# Revit family: 08717100
name_source: partatom
category: Plumbing Fixtures
revit_build: Autodesk Revit 2018 (Build: 20170223_1515(x64)
units: mm (PartAtom-declared; Revit-internal decimal feet)

## family parameters
Always vertical = Yes
Cut with Voids When Loaded = No
OmniClass Number = 23.45.55.00
OmniClass Title = Sanitary Faucets, Wastes
Part Type = Normal
Room Calculation Point = No
Round Connector Dimension = Use Diameter
Shared = No
Work Plane-Based = No

## types (1)
- 08717100 Bath and shower faucet
    2D/3D/BIM Files URL = http://static.hansa.com
    3D View = https://static.hansa.com
    Additional Features = Retrofit safety lock 02000710 against scalding, can be ordered optionally. Limiter adjustable between 38°-42°C during mounting.
    Advanced Features = Inner body made of DZR brass
    Aerator = Standard aerator
    Approval DVGW = NW-6509CR0103
    AssetType = Fixed
    BIMObjectName = 08717100
    Backflow Prevention EN1717 = EB
    BodyMaterial = Brass
    Brand = HANSA
    Catalog Drawing URL = http://static.hansa.com
    Category = Health & Care
    CloseOffRating = 0
    Color = Chrome
    Connection = Eccentric coupling(s);Cover plate(s);Cover plate triple sealed
    Connection Size = G1/2
    Dimension Drawing URL = http://static.hansa.com
    Diverter = Turn operated diverter;Integrated into flow control handle
    DurationUnit = Year
    EAN Number = 4057304013454
    EN Standard = EN 1111
    ETIM Class Number = EC010862 Bath mixing tap
    FDV Document URL = http://www.hansa.com
    FaucetMainMaterial = Brass
    Features = Thermostatic
    Finish = Polished
    Flow Drawing URL = http://static.hansa.com
    Flow Rate At 300kPa = 4030.3 L/s
    FlowCoefficient = 0
    Group = Bath and shower faucet
    IfcExportAs = IfcValveType
    IfcExportType = FAUCET
    Installation Type = Wall mounted
    Installation Width = CC150± 15 mm
    Installation and Maintenance Guide URL = http://static.hansa.com
    Interactive AR View URL = https://static.hansa.com
    Lever Handle = Temperature control handle;Flow control handle;Eco feature for water flow
    Manufacturer = HANSA
    ManufacturerName = HANSA
    ManufacturerURL = http://www.hansa.com
    Market = International;Germany;Austria;Switzerland;Belgium;Netherlands;France;Czech Republic;Slovakia;Italy;Spain;Portugal;Australia
    Material = Brass
    Max. Hot Water Supply = 80 °C
    Mechanical Parts = Ceramic head part for flow control;Thermostatic cartridge for automatic temperature control;Non-return valve(s);Litter filter(s)
    Mobile Product Information URL = http://mpi.hansa.com
    Model = 08717100 Bath and shower faucet
    ModelReference = 08717100
    NBSDescription = Water supply fittings for baths
    NBSReference = 45-35-70/315
    Name = 08717100 Bath and shower faucet
    Name_en = 08717100 Bath and shower faucet
    Noise Class = II (ISO 3822)
    NominalDepth = 183 mm
    NominalHeight = 80 mm  [stored 0.262467 ft]
    NominalWidth = 290 mm
    Product Code = 08717100
    Product Family = HANSACARE Safety
    Product Image URL = http://static.hansa.com
    Product URL = http://static.hansa.com
    Revision = 3
    Sales Package dimensions (LxWxH) = 294 x 164 x 83
    Shape = Sculptured
    Size = 290x185x80 mm
    Spare-Part Information URL = http://static.hansa.com
    Spout Projection = 168 mm
    Spout Type = Fixed spout
    Surface treatment = Chrome
    Technical DataSheet URL = http://www.hansa.com
    Temperature = Temperature limiter (retrofittable);Thermostatic safety stop at 38°C;THERMO COOL
    Temperature Adjustments = Adjustable hot water stop (included, retrofittable);Safety stop against scalding at 38°C;The housing of the fittings conducts minimal heat
    UNSPSC Class Number = 30181700 Faucets or taps
    URL DVGW = http://static.hansa.com
    URL Declaration of Conformity = http://static.hansa.com
    URL REACH = http://static.hansa.com
    Uniclass2 = Pr_40_30_96_10
    Uniclass2015Description = Bath thermostatic water supply sets
    Uniclass2015Reference = Pr_40_20_87_10
    Version = 3
    VersionDate = 01/07/2022
    Warranty Information URL = http://warranty.hansa.com
    WarrantyDescription = http://warranty.hansa.com
    WarrantyDurationUnit = Year
    Working Pressure = 100 - 1000 kPa
    WorkingPressure = 100 - 1000 kPa

note: [stored X ft] marks values corroborated as IEEE doubles in the binary element streams (Revit-internal decimal feet)

## geometry (parser evidence)
native form markers: Sweep x5
no freeform markers — native parametric forms only
